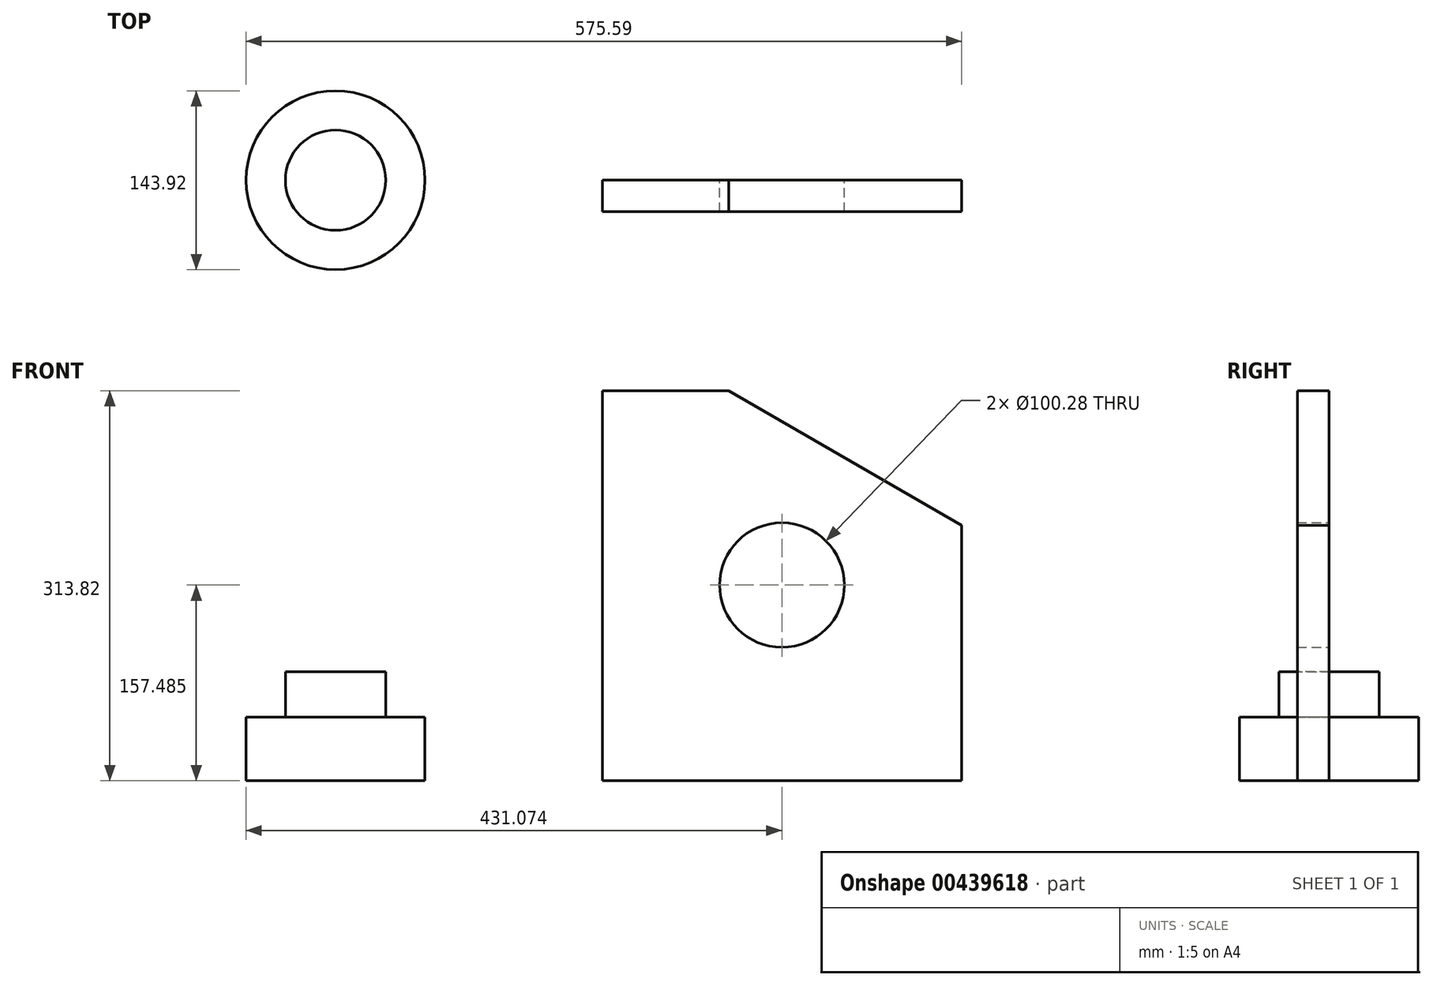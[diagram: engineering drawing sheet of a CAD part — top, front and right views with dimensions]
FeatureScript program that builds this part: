
annotation { "Feature Type Name" : "Feature", "Feature Type Description" : "" }
export const myFeature = defineFeature(function(context is Context, id is Id, definition is map)
    precondition{}
    {
        {
            var Q0;
            Q0=qCreatedBy(makeId("Front.planeOp"),FACE);
            var sketch = newSketch(context, id + "F0", { "sketchPlane" : qUnion([Q0])});
            skLineSegment(sketch, "E0", {"start": v(582.02, 8.6) * mm, "end": v(582.02, 0) * mm});
            skLineSegment(sketch, "E1", {"start": v(0, 0) * mm, "end": v(0, 313.82) * mm});
            skLineSegment(sketch, "E2", {"start": v(0, 313.82) * mm, "end": v(101.6, 313.82) * mm});
            skLineSegment(sketch, "E3", {"start": v(101.6, 313.82) * mm, "end": v(289.03, 205.6) * mm});
            skLineSegment(sketch, "E4", {"start": v(289.03, 205.6) * mm, "end": v(289.03, 0) * mm});
            skLineSegment(sketch, "E5", {"start": v(289.03, 0) * mm, "end": v(0, 0) * mm});
            skCircle(sketch, "E6", {"center": v(144.51, 157.48) * mm, "radius": 50.14 * mm});
            skLineSegment(sketch, "E7", {"start": v(144.51, 157.48) * mm, "end": v(144.51, 0) * mm});
            skSolve(sketch);
        }
        {
            var Q0;
            Q0 = qSketchRegion(id + "F0", true);
            extrude(context, id + "F1", {"entities" : qUnion([Q0]), "depth" : 25.4 * mm});
        }
        {
            var Q0;
            Q0=qCreatedBy(makeId("Front.planeOp"),FACE);
            var sketch = newSketch(context, id + "F2", { "sketchPlane" : qUnion([Q0])});
            skLineSegment(sketch, "E8", {"start": v(-214.6, 0) * mm, "end": v(-214.6, 87.83) * mm});
            skLineSegment(sketch, "E9", {"start": v(-214.6, 87.83) * mm, "end": v(-174.21, 87.83) * mm});
            skLineSegment(sketch, "E10", {"start": v(-174.21, 87.83) * mm, "end": v(-174.21, 51.12) * mm});
            skLineSegment(sketch, "E11", {"start": v(-174.21, 51.12) * mm, "end": v(-142.64, 51.12) * mm});
            skLineSegment(sketch, "E12", {"start": v(-142.64, 51.12) * mm, "end": v(-142.64, 0) * mm});
            skLineSegment(sketch, "E13", {"start": v(-142.64, 0) * mm, "end": v(-214.6, 0) * mm});
            skSolve(sketch);
        }
        {
            var Q0;
            Q0=makeQuery(id+"F2.imprint","IMPRINT",FACE,{"disambiguationData":[TD([[makeQuery(id+"F2.imprint","IMPRINT",EDGE,{"derivedFrom":sQuery(id+"F2.wireOp",EDGE,"E8")}),-1.0]])]});
            var Q1;
            Q1=sQuery(id+"F2.wireOp",EDGE,"E8");
            revolve(context, id + "F3", {"entities" : qUnion([Q0]), "axis" : qUnion([Q1]), "revolveType" : RevolveType.FULL});
        }
    });
